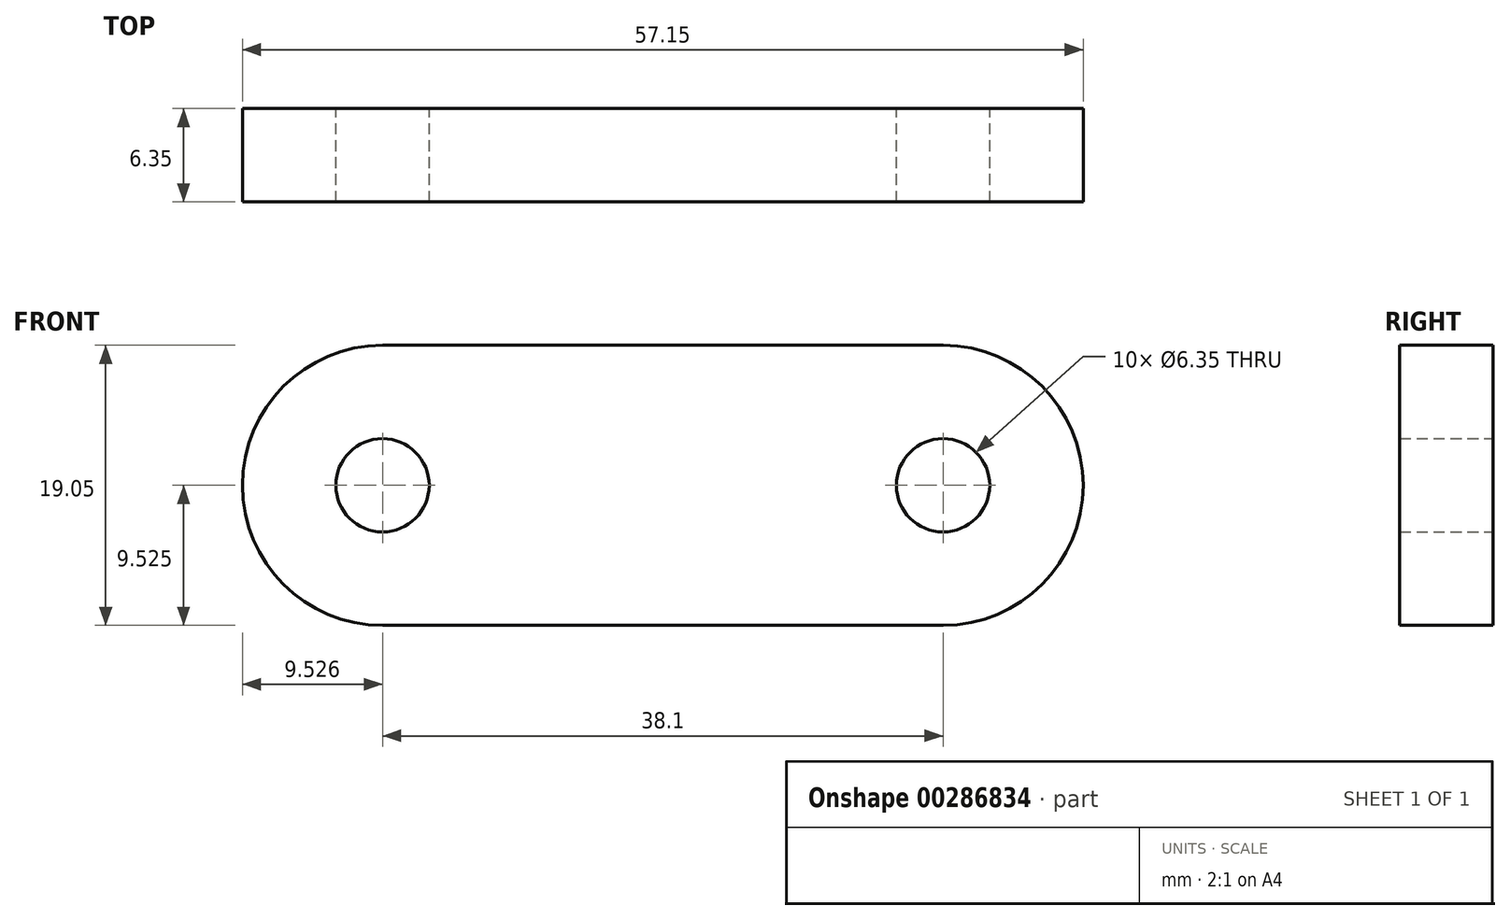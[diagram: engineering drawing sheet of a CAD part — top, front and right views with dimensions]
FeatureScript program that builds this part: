
annotation { "Feature Type Name" : "Feature", "Feature Type Description" : "" }
export const myFeature = defineFeature(function(context is Context, id is Id, definition is map)
    precondition{}
    {
        {
            var Q0;
            Q0=qCreatedBy(makeId("Front.planeOp"),FACE);
            var sketch = newSketch(context, id + "F0", { "sketchPlane" : qUnion([Q0])});
            skLineSegment(sketch, "E0.bottom", {"start": v(-4.7, 6.03) * mm, "end": v(33.4, 6.03) * mm});
            skLineSegment(sketch, "E0.top", {"start": v(-4.7, -13.02) * mm, "end": v(33.4, -13.02) * mm});
            skArc(sketch, "E1", {"start": v(-4.7, 6.03) * mm, "mid": v(-14.23, -3.5) * mm, "end": v(-4.7, -13.02) * mm});
            skArc(sketch, "E2", {"start": v(33.4, -13.02) * mm, "mid": v(42.92, -3.5) * mm, "end": v(33.4, 6.03) * mm});
            skCircle(sketch, "E3", {"center": v(33.4, -3.5) * mm, "radius": 3.18 * mm});
            skCircle(sketch, "E4", {"center": v(-4.7, -3.5) * mm, "radius": 3.18 * mm});
            skSolve(sketch);
        }
        {
            var Q0;
            Q0=makeQuery(id+"F0.imprint","IMPRINT",FACE,{"disambiguationData":[TD([[makeQuery(id+"F0.imprint","IMPRINT",EDGE,{"derivedFrom":sQuery(id+"F0.wireOp",EDGE,"E0.bottom")}),-1.0]])]});
            extrude(context, id + "F1", {"entities" : qUnion([Q0]), "depth" : 6.35 * mm});
        }
    });
